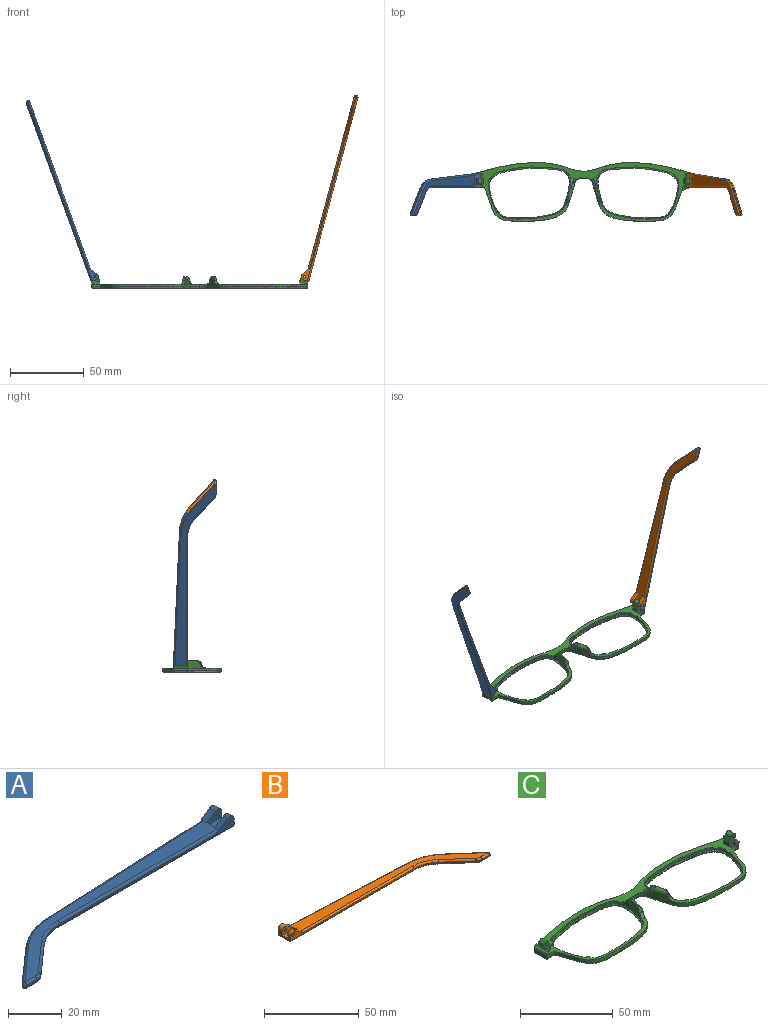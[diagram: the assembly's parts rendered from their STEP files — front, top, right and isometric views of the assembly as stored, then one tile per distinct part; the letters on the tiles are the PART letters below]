
ASSEMBLY  parts=3 mates=2
PART A: 43 faces, bbox 130.2x29.5x5.9 mm
  f0: plane 9.62x3.72mm, normal (1,0,0), area 24.7mm2, adj f1,f3,f4,f5,f10,f16,f18,f28
  f1: cylinder r=2.2mm len=3.45mm, axis (0,-1,0), area 11mm2, adj f0,f2,f4,f37
  f2: plane 6.01x3.91mm, normal (-0.55,0,0.84), area 12.7mm2, adj f1,f4,f9,f19,f37
  f3: plane 2.26x0.1mm, normal (0,0,1), area 0.1mm2, adj f0,f5,f18
  f4: plane 92.1x4.9mm, normal (0,-1,0), area 79.9mm2, adj f0,f1,f2,f14,f19,f36,f42
  f5: plane 93.42x4.13mm, normal (-0.04,1,0), area 64.8mm2, adj f0,f3,f11,f15,f17,f27,f28
  f6: plane 17.82x15.72mm, normal (-0.66,0.75,0), area 14.3mm2, adj f11,f12,f25,f30
  f7: plane 5.46x0.6mm, normal (0,-1,0), area 3.3mm2, adj f12,f13,f23,f32
  f8: plane 14.99x13.23mm, normal (0.66,-0.75,0), area 12mm2, adj f13,f14,f21,f34
  f9: plane 121.18x26.73mm, normal (0,0,1), area 627.7mm2, adj f2,f17,f19,f20,f21,f22,f23,f25
  f10: plane 129.1x27.08mm, normal (0,0,-1), area 686.5mm2, adj f0,f28,f29,f30,f32,f33,f34,f35
  f11: cylinder r=30mm len=18.52mm, axis (0,0,-1), area 12.2mm2, adj f5,f6,f26,f29
  f12: cylinder r=1mm len=1.75mm, axis (0,0,-1), area 1.5mm2, adj f6,f7,f24,f31
  f13: cylinder r=5mm len=3.31mm, axis (0,0,-1), area 2.2mm2, adj f7,f8,f22,f33
  f14: cylinder r=20mm len=13.23mm, axis (0,0,1), area 8.7mm2, adj f4,f8,f20,f35
  f15: plane 5.66x0.25mm, normal (0,0,-1), area 0.7mm2, adj f5,f17,f18
  f16: cylinder r=2.2mm len=3.45mm, axis (0,-1,0), area 14.8mm2, adj f0,f17,f18,f38
  f17: plane 6.01x3.91mm, normal (-0.55,0,0.84), area 16.9mm2, adj f5,f9,f15,f16,f18,f27,f38
  f18: plane 7.92x3.3mm, normal (0,1,0), area 15.9mm2, adj f0,f3,f15,f16,f17,f41
  f19: cylinder r=1mm len=84.18mm, axis (-1,0,0), area 131.4mm2, adj f2,f4,f9,f20
  f20: torus R=21mm, axis (0,0,1), area 23.1mm2, adj f9,f14,f19,f21
  f21: cylinder r=1mm len=15.65mm, axis (-0.75,-0.66,0), area 31.4mm2, adj f8,f9,f20,f22
  f22: torus R=4mm, axis (0,0,1), area 5.3mm2, adj f9,f13,f21,f23
  f23: cylinder r=1mm len=5.46mm, axis (-1,0,0), area 8.6mm2, adj f7,f9,f22,f24
  f24: sphere r=1mm, area 2.4mm2, adj f12,f23,f25
  f25: cylinder r=1mm len=18.48mm, axis (0.75,0.66,0), area 37.3mm2, adj f6,f9,f24,f26
  f26: torus R=29mm, axis (0,0,1), area 31.6mm2, adj f9,f11,f25,f27
  f27: cylinder r=1mm len=85.5mm, axis (1,0.04,0), area 133.5mm2, adj f5,f9,f17,f26
  f28: cylinder r=1mm len=93.46mm, axis (-1,-0.04,0), area 146.9mm2, adj f0,f5,f10,f29
  f29: torus R=29mm, axis (0,0,1), area 31.6mm2, adj f10,f11,f28,f30
  f30: cylinder r=1mm len=18.48mm, axis (-0.75,-0.66,0), area 37.3mm2, adj f6,f10,f29,f31
  f31: sphere r=1mm, area 2.4mm2, adj f12,f30,f32
  f32: cylinder r=1mm len=5.46mm, axis (1,0,0), area 8.6mm2, adj f7,f10,f31,f33
  f33: torus R=4mm, axis (0,0,1), area 5.3mm2, adj f10,f13,f32,f34
  f34: cylinder r=1mm len=15.65mm, axis (0.75,0.66,0), area 31.4mm2, adj f8,f10,f33,f35
  f35: torus R=21mm, axis (0,0,1), area 23.1mm2, adj f10,f14,f34,f36
  f36: cylinder r=1mm len=92.1mm, axis (1,0,0), area 144.7mm2, adj f0,f4,f10,f35
  f37: plane 7.92x4.7mm, normal (0,1,0), area 27mm2, adj f0,f1,f2,f39,f40,f42
  f38: plane 7.92x4.7mm, normal (0,-1,0), area 27mm2, adj f0,f16,f17,f39,f40,f41
  f39: plane 7.92x4.1mm, normal (0,0,1), area 32.5mm2, adj f0,f37,f38,f40
  f40: plane 4.1x1.4mm, normal (1,0,0), area 5.7mm2, adj f9,f37,f38,f39
  f41: cylinder r=0.5mm len=3.1mm, axis (0,-1,0), area 9.7mm2, adj f18,f38
  f42: cylinder r=0.5mm len=2.3mm, axis (0,-1,0), area 7.2mm2, adj f4,f37
PART B: 43 faces, bbox 130.2x29.5x5.9 mm
  f0: plane 9.62x3.72mm, normal (-1,0,0), area 24.7mm2, adj f1,f3,f4,f5,f10,f16,f18,f28
  f1: cylinder r=2.2mm len=3.45mm, axis (0,-1,0), area 11mm2, adj f0,f2,f4,f37
  f2: plane 6.01x3.91mm, normal (0.55,0,0.84), area 12.7mm2, adj f1,f4,f9,f19,f37
  f3: plane 2.26x0.1mm, normal (0,0,1), area 0.1mm2, adj f0,f5,f18
  f4: plane 92.1x4.9mm, normal (0,-1,0), area 78.2mm2, adj f0,f1,f2,f14,f19,f36,f42
  f5: plane 93.42x4.13mm, normal (0.04,1,0), area 64.8mm2, adj f0,f3,f11,f15,f17,f27,f28
  f6: plane 17.82x15.72mm, normal (0.66,0.75,0), area 14.3mm2, adj f11,f12,f25,f30
  f7: plane 5.46x0.6mm, normal (0,-1,0), area 3.3mm2, adj f12,f13,f23,f32
  f8: plane 14.99x13.23mm, normal (-0.66,-0.75,0), area 12mm2, adj f13,f14,f21,f34
  f9: plane 121.18x26.73mm, normal (0,0,1), area 627.7mm2, adj f2,f17,f19,f20,f21,f22,f23,f25
  f10: plane 129.1x27.08mm, normal (0,0,-1), area 686.5mm2, adj f0,f28,f29,f30,f32,f33,f34,f35
  f11: cylinder r=30mm len=18.52mm, axis (0,0,-1), area 12.2mm2, adj f5,f6,f26,f29
  f12: cylinder r=1mm len=1.75mm, axis (0,0,-1), area 1.5mm2, adj f6,f7,f24,f31
  f13: cylinder r=5mm len=3.31mm, axis (0,0,-1), area 2.2mm2, adj f7,f8,f22,f33
  f14: cylinder r=20mm len=13.23mm, axis (0,0,1), area 8.7mm2, adj f4,f8,f20,f35
  f15: plane 5.66x0.25mm, normal (0,0,-1), area 0.7mm2, adj f5,f17,f18
  f16: cylinder r=2.2mm len=3.45mm, axis (0,-1,0), area 14.8mm2, adj f0,f17,f18,f38
  f17: plane 6.01x3.91mm, normal (0.55,0,0.84), area 16.9mm2, adj f5,f9,f15,f16,f18,f27,f38
  f18: plane 7.92x3.3mm, normal (0,1,0), area 14.3mm2, adj f0,f3,f15,f16,f17,f41
  f19: cylinder r=1mm len=84.18mm, axis (1,0,0), area 131.4mm2, adj f2,f4,f9,f20
  f20: torus R=21mm, axis (0,0,1), area 23.1mm2, adj f9,f14,f19,f21
  f21: cylinder r=1mm len=15.65mm, axis (0.75,-0.66,0), area 31.4mm2, adj f8,f9,f20,f22
  f22: torus R=4mm, axis (0,0,1), area 5.3mm2, adj f9,f13,f21,f23
  f23: cylinder r=1mm len=5.46mm, axis (1,0,0), area 8.6mm2, adj f7,f9,f22,f24
  f24: sphere r=1mm, area 2.4mm2, adj f12,f23,f25
  f25: cylinder r=1mm len=18.48mm, axis (-0.75,0.66,0), area 37.3mm2, adj f6,f9,f24,f26
  f26: torus R=29mm, axis (0,0,1), area 31.6mm2, adj f9,f11,f25,f27
  f27: cylinder r=1mm len=85.5mm, axis (-1,0.04,0), area 133.5mm2, adj f5,f9,f17,f26
  f28: cylinder r=1mm len=93.46mm, axis (1,-0.04,0), area 146.9mm2, adj f0,f5,f10,f29
  f29: torus R=29mm, axis (0,0,1), area 31.6mm2, adj f10,f11,f28,f30
  f30: cylinder r=1mm len=18.48mm, axis (0.75,-0.66,0), area 37.3mm2, adj f6,f10,f29,f31
  f31: sphere r=1mm, area 2.4mm2, adj f12,f30,f32
  f32: cylinder r=1mm len=5.46mm, axis (-1,0,0), area 8.6mm2, adj f7,f10,f31,f33
  f33: torus R=4mm, axis (0,0,1), area 5.3mm2, adj f10,f13,f32,f34
  f34: cylinder r=1mm len=15.65mm, axis (-0.75,0.66,0), area 31.4mm2, adj f8,f10,f33,f35
  f35: torus R=21mm, axis (0,0,1), area 23.1mm2, adj f10,f14,f34,f36
  f36: cylinder r=1mm len=92.1mm, axis (-1,0,0), area 144.7mm2, adj f0,f4,f10,f35
  f37: plane 7.92x4.7mm, normal (0,1,0), area 25.4mm2, adj f0,f1,f2,f39,f40,f42
  f38: plane 7.92x4.7mm, normal (0,-1,0), area 25.4mm2, adj f0,f16,f17,f39,f40,f41
  f39: plane 7.92x4.1mm, normal (0,0,1), area 32.5mm2, adj f0,f37,f38,f40
  f40: plane 4.1x1.4mm, normal (-1,0,0), area 5.7mm2, adj f9,f37,f38,f39
  f41: cylinder r=0.88mm len=3.1mm, axis (0,-1,0), area 17mm2, adj f18,f38
  f42: cylinder r=0.88mm len=2.3mm, axis (0,-1,0), area 12.6mm2, adj f4,f37
PART C: 118 faces, bbox 148.1x40.9x17.9 mm
  f0: bspline ~1.82x1.22mm, area 0.7mm2, adj f2,f7,f37,f52
  f1: plane 147.69x40.46mm, normal (0,0,1), area 858.2mm2, adj f4,f5,f6,f7,f8,f12,f20,f23
  f2: bspline ~6.1x4.93mm, area 12.7mm2, adj f0,f7,f37,f41,f43,f52,f53
  f3: plane 4.46x1.45mm, normal (0,0,1), area 0.1mm2, adj f7,f38
  f4: plane 1.23x0.04mm, normal (0,0,1), area 0mm2, adj f1,f7,f22
  f5: plane 6.97x5.07mm, normal (0,1,0), area 22.7mm2, adj f1,f20,f21,f25,f27,f28,f30,f31
  f6: plane 3.2x2.36mm, normal (0,-1,0), area 5.7mm2, adj f1,f20,f26,f29
  f7: extruded ~73.26x39.84mm, area 292.7mm2, adj f0,f1,f2,f3,f4,f8,f13,f14
  f8: extruded ~35.39x5.69mm, area 72.2mm2, adj f1,f7,f18,f67
  f9: plane 144.78x37.85mm, normal (0,0,-1), area 582.4mm2, adj f13,f15,f17,f18,f19,f71,f73,f75
  f10: plane 56.06x35.45mm, normal (0,0,1), area 127mm2, adj f11,f19
  f11: extruded ~55.69x35.36mm, area 160.5mm2, adj f10,f12
  f12: extruded ~55.69x35.36mm, area 226.3mm2, adj f1,f11,f39,f40,f41,f42,f43,f44
  f13: bspline ~73.27x30.39mm, area 161.7mm2, adj f7,f9,f14,f71
  f14: bspline ~1x1mm, area 0.8mm2, adj f7,f13,f15
  f15: bspline ~8.99x1.23mm, area 12.6mm2, adj f7,f9,f14,f16
  f16: bspline ~1.04x1mm, area 0.7mm2, adj f7,f15,f17
  f17: bspline ~45.86x8.59mm, area 59.8mm2, adj f7,f9,f16,f18
  f18: bspline ~37.01x6.7mm, area 56.6mm2, adj f8,f9,f17,f76
  f19: bspline ~56.23x35.9mm, area 235.3mm2, adj f9,f10
  f20: plane 4x2.36mm, normal (-1,0,0), area 9.5mm2, adj f1,f5,f6,f21
  f21: plane 4x0.02mm, normal (0.34,0,0.94), area 0.1mm2, adj f5,f20,f28
  f22: plane 2.76x2.53mm, normal (0,-1,0), area 3.9mm2, adj f4,f26,f27,f35,f56
  f23: plane 7.67x1.6mm, normal (0.94,0,-0.34), area 13mm2, adj f1,f35,f36,f56
  f24: plane 2.1x1.69mm, normal (0,1,0), area 2.8mm2, adj f1,f25,f27,f36,f56
  f25: plane 3.3x2.1mm, normal (-1,0,0), area 6.9mm2, adj f1,f5,f24,f27
  f26: plane 2.35x2.1mm, normal (-1,0,0), area 4.9mm2, adj f1,f6,f22,f27,f29
  f27: plane 9.65x1.24mm, normal (0,0,1), area 8.2mm2, adj f5,f22,f24,f25,f26,f29,f30,f56
  f28: plane 4x3.31mm, normal (-0.94,0,0.34), area 14.1mm2, adj f5,f21,f29,f32
  f29: plane 5.77x5.06mm, normal (0,-1,0), area 17mm2, adj f6,f26,f27,f28,f30,f31,f32,f33
  f30: plane 4x2.21mm, normal (0.94,0,-0.34), area 9.4mm2, adj f5,f27,f29,f33
  f31: plane 4x0.01mm, normal (0.34,0,0.94), area 0mm2, adj f5,f29,f32,f33
  f32: cylinder r=1.98mm len=4mm, axis (0,1,0), area 12.4mm2, adj f5,f28,f29,f31
  f33: cylinder r=1.98mm len=4mm, axis (0,-1,0), area 12.4mm2, adj f5,f29,f30,f31
  f34: cylinder r=0.88mm len=4mm, axis (0,-1,0), area 22mm2, adj f5,f29
  f35: cone r=1mm half-angle=20deg, axis (0,0,1), area 2.3mm2, adj f1,f22,f23,f56
  f36: cylinder r=1mm len=2.28mm, axis (-0.34,0,-0.94), area 3mm2, adj f1,f23,f24,f56
  f37: extruded ~3.67x3.11mm, area 5.9mm2, adj f0,f2,f7,f59
  f38: extruded ~4.44x3.32mm, area 15.1mm2, adj f3,f7,f42,f43,f55
  f39: extruded ~4.98x1.37mm, area 6.6mm2, adj f12,f41
  f40: plane 3.63x0.97mm, normal (0,0,1), area 0.3mm2, adj f12,f41,f43
  f41: bspline ~15.5x15.35mm, area 6.4mm2, adj f2,f12,f39,f40,f54
  f42: bspline ~7.26x7.26mm, area 6.3mm2, adj f12,f38,f43,f55
  f43: bspline ~10.29x4.84mm, area 21.4mm2, adj f2,f7,f12,f38,f40,f42
  f44: plane 3.19x1.37mm, normal (0,0,-1), area 2.1mm2, adj f12,f45
  f45: cylinder r=2.28mm len=3.17mm, axis (0,0,1), area 2.1mm2, adj f1,f12,f44,f54
  f46: plane 3.14x2.79mm, normal (0,0,-1), area 3.9mm2, adj f12,f47
  f47: cylinder r=2.28mm len=3.13mm, axis (0,0,1), area 2.5mm2, adj f1,f12,f46
  f48: plane 1.79x1.31mm, normal (0,0,-1), area 0.9mm2, adj f12,f49
  f49: cylinder r=1.3mm len=1.78mm, axis (0,0,1), area 1.3mm2, adj f1,f12,f48
  f50: plane 1.95x1.68mm, normal (0,0,-1), area 1.5mm2, adj f12,f51
  f51: cylinder r=1.3mm len=1.93mm, axis (0,0,1), area 1.5mm2, adj f1,f12,f50
  f52: bspline ~2.66x2.04mm, area 1.9mm2, adj f0,f2,f7,f53,f58
  f53: bspline ~3.55x3.47mm, area 3.7mm2, adj f1,f2,f52,f54,f58
  f54: bspline ~6.16x4.45mm, area 7.9mm2, adj f1,f12,f41,f45,f53
  f55: bspline ~3.7x3.66mm, area 7.8mm2, adj f1,f7,f12,f38,f42
  f56: plane 9.71x1.44mm, normal (0.34,0,0.94), area 13.9mm2, adj f22,f23,f24,f27,f35,f36
  f57: bspline ~6.38x2.14mm, area 2.6mm2, adj f1,f7,f58,f115
  f58: bspline ~2.1x1.46mm, area 0.6mm2, adj f7,f52,f53,f57
  f59: bspline ~5.24x1.75mm, area 0mm2, adj f7,f37
  f60: bspline ~2.19x1.4mm, area 0.7mm2, adj f61,f66,f95,f110
  f61: bspline ~6.1x4.93mm, area 12.6mm2, adj f60,f66,f95,f99,f101,f110,f111
  f62: plane 4.46x1.45mm, normal (0,0,1), area 0.1mm2, adj f66,f96
  f63: plane 1.23x0.04mm, normal (0,0,1), area 0mm2, adj f1,f66,f80
  f64: plane 6.97x5.07mm, normal (0,1,0), area 22.7mm2, adj f1,f78,f79,f83,f85,f86,f88,f89
  f65: plane 3.2x2.36mm, normal (0,-1,0), area 5.7mm2, adj f1,f78,f84,f87
  f66: extruded ~73.26x39.84mm, area 292.7mm2, adj f1,f7,f60,f61,f62,f63,f67,f71
  f67: extruded ~35.39x5.69mm, area 72.2mm2, adj f1,f8,f66,f76
  f68: plane 56.06x35.45mm, normal (0,0,1), area 127mm2, adj f69,f77
  f69: extruded ~55.69x35.36mm, area 160.5mm2, adj f68,f70
  f70: extruded ~55.69x35.36mm, area 226.4mm2, adj f1,f69,f97,f98,f99,f100,f101,f102
  f71: bspline ~73.83x30.39mm, area 161.7mm2, adj f9,f13,f66,f72
  f72: bspline ~1x1mm, area 0.8mm2, adj f66,f71,f73
  f73: bspline ~8.99x1.23mm, area 12.6mm2, adj f9,f66,f72,f74
  f74: bspline ~1.04x1mm, area 0.8mm2, adj f66,f73,f75
  f75: bspline ~45.86x8.59mm, area 59.8mm2, adj f9,f66,f74,f76
  f76: bspline ~37.01x6.7mm, area 56.6mm2, adj f9,f18,f67,f75
  f77: bspline ~56.22x35.9mm, area 235.3mm2, adj f9,f68
  f78: plane 4x2.36mm, normal (1,0,0), area 9.5mm2, adj f1,f64,f65,f79
  f79: plane 4x0.02mm, normal (-0.34,0,0.94), area 0.1mm2, adj f64,f78,f86
  f80: plane 2.76x2.53mm, normal (0,-1,0), area 3.9mm2, adj f63,f84,f85,f93,f114
  f81: plane 7.67x1.6mm, normal (-0.94,0,-0.34), area 13mm2, adj f1,f93,f94,f114
  f82: plane 2.1x1.69mm, normal (0,1,0), area 2.8mm2, adj f1,f83,f85,f94,f114
  f83: plane 3.3x2.1mm, normal (1,0,0), area 6.9mm2, adj f1,f64,f82,f85
  f84: plane 2.35x2.1mm, normal (1,0,0), area 4.9mm2, adj f1,f65,f80,f85,f87
  f85: plane 9.65x1.24mm, normal (0,0,1), area 8.2mm2, adj f64,f80,f82,f83,f84,f87,f88,f114
  f86: plane 4x3.31mm, normal (0.94,0,0.34), area 14.1mm2, adj f64,f79,f87,f90
  f87: plane 5.77x5.06mm, normal (0,-1,0), area 17mm2, adj f65,f84,f85,f86,f88,f89,f90,f91
  f88: plane 4x2.21mm, normal (-0.94,0,-0.34), area 9.4mm2, adj f64,f85,f87,f91
  f89: plane 4x0.01mm, normal (-0.34,0,0.94), area 0mm2, adj f64,f87,f90,f91
  f90: cylinder r=1.98mm len=4mm, axis (0,1,0), area 12.4mm2, adj f64,f86,f87,f89
  f91: cylinder r=1.98mm len=4mm, axis (0,-1,0), area 12.4mm2, adj f64,f87,f88,f89
  f92: cylinder r=0.88mm len=4mm, axis (0,-1,0), area 22mm2, adj f64,f87
  f93: cone r=1mm half-angle=20deg, axis (0,0,1), area 2.3mm2, adj f1,f80,f81,f114
  f94: cylinder r=1mm len=2.28mm, axis (0.34,0,-0.94), area 3mm2, adj f1,f81,f82,f114
  f95: extruded ~3.67x3.11mm, area 5.9mm2, adj f60,f61,f66,f117
  f96: extruded ~4.44x3.32mm, area 15.1mm2, adj f62,f66,f100,f101,f113
  f97: extruded ~4.98x1.36mm, area 6.6mm2, adj f70,f99
  f98: plane 3.63x0.97mm, normal (0,0,1), area 0.3mm2, adj f70,f99,f101
  f99: bspline ~15.5x15.35mm, area 6.4mm2, adj f61,f70,f97,f98,f112
  f100: bspline ~7.26x7.26mm, area 6.2mm2, adj f70,f96,f101,f113
  f101: bspline ~10.29x4.84mm, area 21.5mm2, adj f61,f66,f70,f96,f98,f100
  f102: plane 3.19x1.37mm, normal (0,0,-1), area 2.1mm2, adj f70,f103
  f103: cylinder r=2.28mm len=3.17mm, axis (0,0,1), area 2.1mm2, adj f1,f70,f102,f112
  f104: plane 3.14x2.79mm, normal (0,0,-1), area 3.9mm2, adj f70,f105
  f105: cylinder r=2.28mm len=3.13mm, axis (0,0,1), area 2.5mm2, adj f1,f70,f104
  f106: plane 1.79x1.31mm, normal (0,0,-1), area 0.9mm2, adj f70,f107
  f107: cylinder r=1.3mm len=1.78mm, axis (0,0,1), area 1.3mm2, adj f1,f70,f106
  f108: plane 1.95x1.68mm, normal (0,0,-1), area 1.5mm2, adj f70,f109
  f109: cylinder r=1.3mm len=1.93mm, axis (0,0,1), area 1.5mm2, adj f1,f70,f108
  f110: bspline ~2.65x2.03mm, area 1.9mm2, adj f60,f61,f66,f111,f116
  f111: bspline ~3.55x3.47mm, area 3.7mm2, adj f1,f61,f110,f112,f116
  f112: bspline ~5.94x4.42mm, area 7.9mm2, adj f1,f70,f99,f103,f111
  f113: bspline ~3.7x3.66mm, area 7.8mm2, adj f1,f66,f70,f96,f100
  f114: plane 9.71x1.44mm, normal (-0.34,0,0.94), area 13.9mm2, adj f80,f81,f82,f85,f93,f94
  f115: bspline ~6.38x2.14mm, area 2.6mm2, adj f1,f57,f66,f116
  f116: bspline ~2.1x1.46mm, area 0.6mm2, adj f66,f110,f111,f115
  f117: bspline ~5.24x1.75mm, area 0mm2, adj f66,f95
PLACE A rot(axis=(0,1,0),70deg) t=(-111.99,-16.07,64.09)mm
PLACE B rot(axis=(0,-1,0),75deg) t=(40.98,-16.07,-53.52)mm
PLACE C t=(-17.07,-11.46,2.31)mm fixed
MATE revolute A.f1 <-> C.f90  axis (0,-1,0) through (-88.11,-7.61,9.3)mm
MATE revolute B.f41 <-> C.f33  axis (0,-1,0) through (53.98,-7.61,9.3)mm
